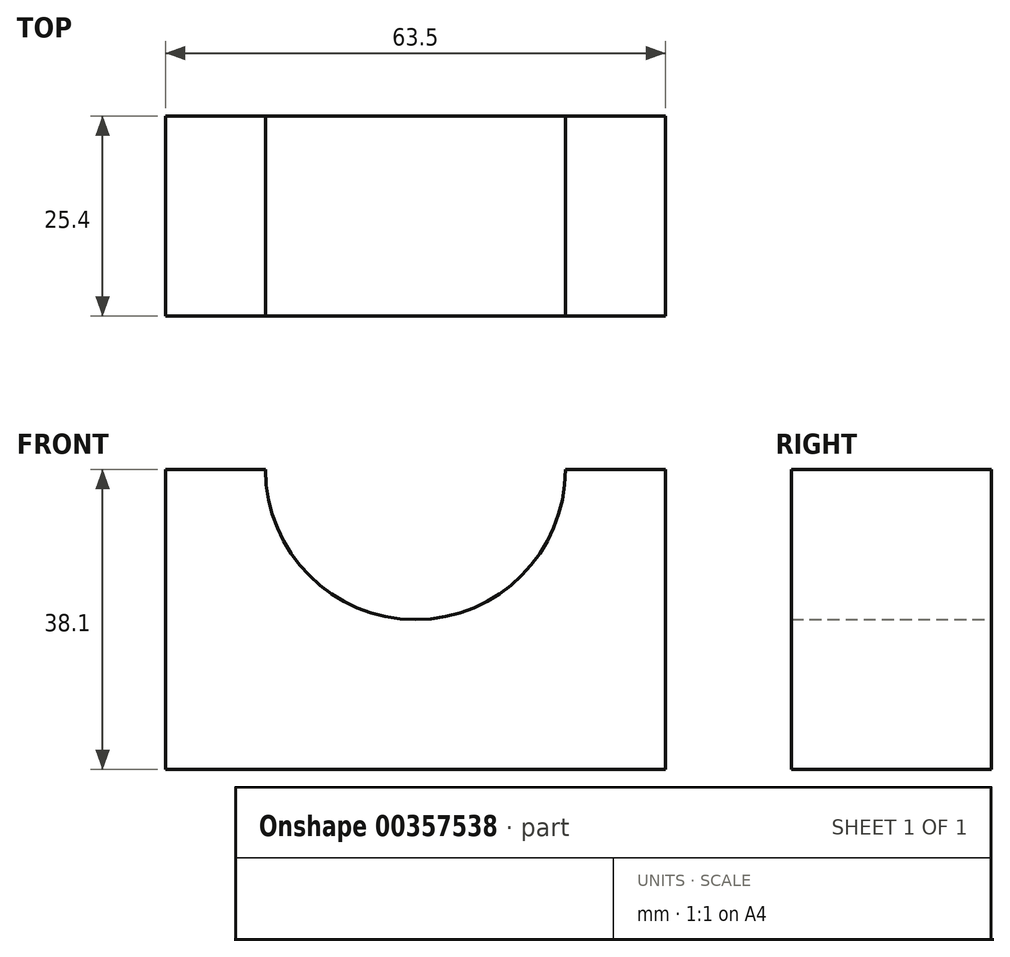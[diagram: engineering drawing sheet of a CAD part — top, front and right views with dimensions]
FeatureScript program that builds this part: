
annotation { "Feature Type Name" : "Feature", "Feature Type Description" : "" }
export const myFeature = defineFeature(function(context is Context, id is Id, definition is map)
    precondition{}
    {
        {
            var Q0;
            Q0=qCreatedBy(makeId("Front.planeOp"),FACE);
            var sketch = newSketch(context, id + "F0", { "sketchPlane" : qUnion([Q0])});
            skLineSegment(sketch, "E0", {"start": v(-74.94, 47.12) * mm, "end": v(-11.44, 47.12) * mm});
            skLineSegment(sketch, "E1", {"start": v(-11.44, 47.12) * mm, "end": v(-11.44, 9.02) * mm});
            skLineSegment(sketch, "E2", {"start": v(-11.44, 9.02) * mm, "end": v(-74.94, 9.02) * mm});
            skLineSegment(sketch, "E3", {"start": v(-74.94, 9.02) * mm, "end": v(-74.94, 47.12) * mm});
            skLineSegment(sketch, "E4", {"start": v(-74.94, 9.02) * mm, "end": v(-43.2, 9.02) * mm});
            skLineSegment(sketch, "E5", {"start": v(-43.2, 9.02) * mm, "end": v(-43.2, 28.07) * mm});
            skLineSegment(sketch, "E6", {"start": v(-11.44, 47.12) * mm, "end": v(-24.14, 47.12) * mm});
            skLineSegment(sketch, "E7", {"start": v(-74.94, 47.12) * mm, "end": v(-62.24, 47.12) * mm});
            skArc(sketch, "E8", {"start": v(-62.24, 47.12) * mm, "mid": v(-43.2, 28.07) * mm, "end": v(-24.14, 47.12) * mm});
            skSolve(sketch);
        }
        {
            var Q0;
            Q0=makeQuery(id+"F0.imprint","IMPRINT",FACE,{"disambiguationData":[TD([[makeQuery(id+"F0.imprint","IMPRINT",EDGE,{"derivedFrom":sQuery(id+"F0.wireOp",EDGE,"E3")}),-1.0]])]});
            var Q1;
            Q1=makeQuery(id+"F0.imprint","IMPRINT",FACE,{"disambiguationData":[TD([[makeQuery(id+"F0.imprint","IMPRINT",EDGE,{"derivedFrom":sQuery(id+"F0.wireOp",EDGE,"E1")}),-1.0]])]});
            extrude(context, id + "F1", {"entities" : qUnion([Q0, Q1]), "depth" : 25.4 * mm});
        }
    });
